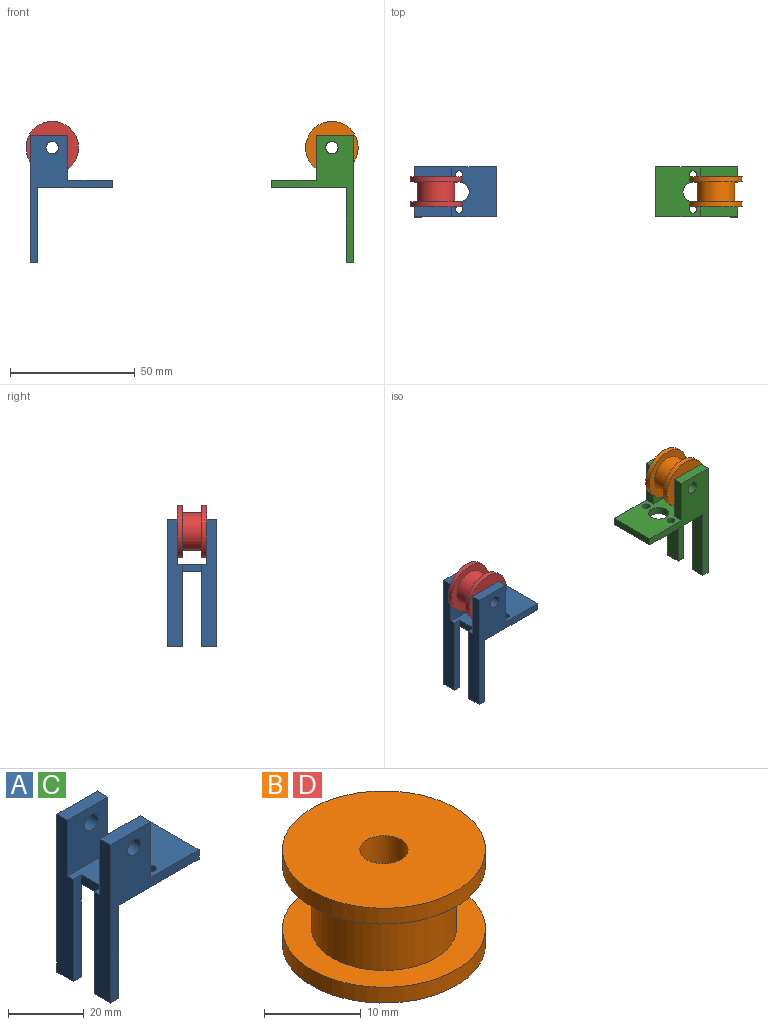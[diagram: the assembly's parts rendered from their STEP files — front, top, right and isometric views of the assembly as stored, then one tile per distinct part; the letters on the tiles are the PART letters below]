
ASSEMBLY  parts=4 mates=6
PART A: 25 faces, bbox 33x20x51 mm
  f0: plane 51x6mm, normal (-1,0,0), area 270mm2, adj f1,f3,f10,f15,f17,f18
  f1: plane 6x3mm, normal (0,0,-1), area 18mm2, adj f0,f6,f10,f15
  f2: plane 30x6mm, normal (1,0,0), area 180mm2, adj f5,f7,f9,f16
  f3: plane 33x20mm, normal (0,0,1), area 451.6mm2, adj f0,f4,f8,f9,f10,f11,f12,f13
  f4: plane 51x6mm, normal (-1,0,0), area 270mm2, adj f3,f5,f9,f16,f20,f21
  f5: plane 6x3mm, normal (0,0,-1), area 18mm2, adj f2,f4,f9,f16
  f6: plane 30x6mm, normal (1,0,0), area 180mm2, adj f1,f7,f10,f15
  f7: plane 30x20mm, normal (0,0,-1), area 535.6mm2, adj f2,f6,f8,f9,f10,f11,f12,f13
  f8: plane 20x3mm, normal (1,0,0), area 60mm2, adj f3,f7,f9,f10
  f9: plane 51x33mm, normal (0,-1,0), area 439.4mm2, adj f2,f3,f4,f5,f7,f8,f21,f22
  f10: plane 51x33mm, normal (0,1,0), area 439.4mm2, adj f0,f1,f3,f6,f7,f8,f18,f19
  f11: cylinder r=4mm len=8mm, axis (0,0,1), area 75.4mm2, adj f3,f7
  f12: cylinder r=1.5mm len=3mm, axis (0,0,1), area 28.3mm2, adj f3,f7
  f13: cylinder r=1.5mm len=3mm, axis (0,0,1), area 28.3mm2, adj f3,f7
  f14: plane 8x3mm, normal (-1,0,0), area 24mm2, adj f3,f7,f15,f16
  f15: plane 33x3mm, normal (0,-1,0), area 99mm2, adj f0,f1,f3,f6,f14
  f16: plane 33x3mm, normal (0,1,0), area 99mm2, adj f2,f3,f4,f5,f14
  f17: plane 18x15mm, normal (0,-1,0), area 250.4mm2, adj f0,f3,f18,f19,f24
  f18: plane 15x4mm, normal (0,0,1), area 60mm2, adj f0,f10,f17,f19
  f19: plane 18x4mm, normal (1,0,0), area 72mm2, adj f3,f10,f17,f18
  f20: plane 18x15mm, normal (0,1,0), area 250.4mm2, adj f3,f4,f21,f22,f23
  f21: plane 15x4mm, normal (0,0,1), area 60mm2, adj f4,f9,f20,f22
  f22: plane 18x4mm, normal (1,0,0), area 72mm2, adj f3,f9,f20,f21
  f23: cylinder r=2.5mm len=5mm, axis (0,-1,0), area 62.8mm2, adj f9,f20
  f24: cylinder r=2.5mm len=5mm, axis (0,-1,0), area 62.8mm2, adj f10,f17
PART B: 8 faces, bbox 21x21x12 mm
  f0: plane 21x21mm, normal (0,0,-1), area 326.7mm2, adj f1,f7
  f1: cylinder r=2.5mm len=12mm, axis (0,0,-1), area 188.5mm2, adj f0,f2
  f2: plane 21x21mm, normal (0,0,1), area 326.7mm2, adj f1,f3
  f3: cylinder r=10.5mm len=21mm, axis (0,0,-1), area 131.9mm2, adj f2,f4
  f4: plane 21x21mm, normal (0,0,-1), area 169.6mm2, adj f3,f5
  f5: cylinder r=7.5mm len=15mm, axis (0,0,-1), area 377mm2, adj f4,f6
  f6: plane 21x21mm, normal (0,0,1), area 169.6mm2, adj f5,f7
  f7: cylinder r=10.5mm len=21mm, axis (0,0,-1), area 131.9mm2, adj f0,f6
PART C: same geometry as A
PART D: same geometry as B
PLACE A t=(-60.53,19.33,-16.43)mm
PLACE B rot(axis=(1,0,0),90deg) t=(60.25,25.33,29.57)mm
PLACE C rot(axis=(0,0,1),180deg) t=(69.08,19.33,-16.43)mm
PLACE D rot(axis=(-1,0,0),90deg) t=(-51.7,13.33,29.57)mm
MATE planar C.f9 <-> A.f10  axis (0,1,0) through (66.08,29.33,13.57)mm
MATE cylindrical D.f1 <-> A.f23  axis (0,-1,0) through (-51.7,23.33,29.57)mm
MATE planar C.f1 <-> A.f1  axis (0,0,-1) through (67.58,12.33,-16.43)mm
MATE cylindrical B.f1 <-> C.f23  axis (0,1,0) through (60.25,19.33,29.57)mm
MATE planar D.f1 <-> A.f20  axis (0,-1,0) through (-51.7,13.33,29.57)mm
MATE planar B.f1 <-> D.f1  axis (0,-1,0) through (60.25,13.33,29.57)mm
